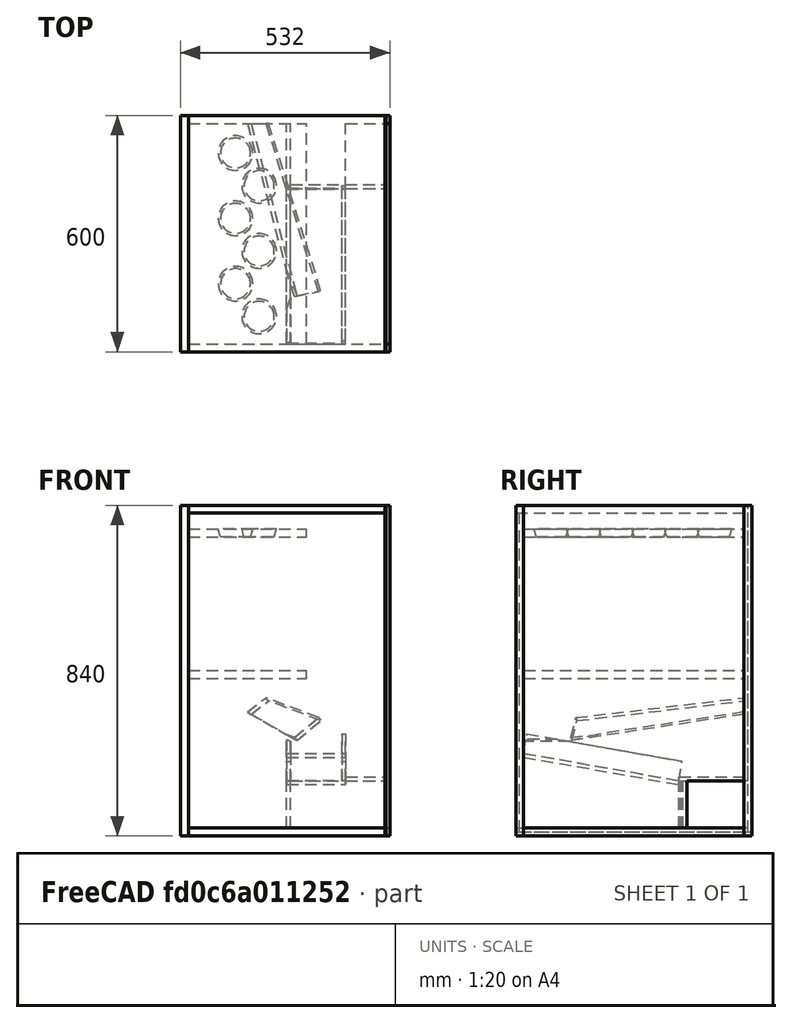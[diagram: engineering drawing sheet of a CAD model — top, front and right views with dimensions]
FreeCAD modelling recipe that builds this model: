
FCSTD DOCUMENT  (FreeCAD 0.16R)
Label: Structure
License: All rights reserved
LicenseURL: http://en.wikipedia.org/wiki/All_rights_reserved
objects: Part::Box×23, Part::FeaturePython×10, Part::Cone×6
note: 39 computed .brp shape members not serialized (recipe doc carries the construction recipe); baked Part::Feature solids carry a one-line shape summary decoded from their .brp

FEATURE [Part::Box] Box  label="bottom"
  Height = 20
  Length = 500
  Width = 600
FEATURE [Part::Box] Box001  label="left"
  Height = 800
  Length = 500
  Placement = pos=(0,0,20) rot=(0,0,1;0rad)
  Width = 20
FEATURE [Part::Box] Box002  label="right"
  Height = 800
  Length = 500
  Placement = pos=(0,580,20) rot=(0,0,1;0rad)
  Width = 20
FEATURE [Part::Box] Box003  label="top"
  Height = 20
  Length = 500
  Placement = pos=(0,0,820) rot=(0,0,1;0rad)
  Width = 600
FEATURE [Part::Box] Box004  label="shelf"
  Height = 20
  Length = 300
  Placement = pos=(0,20,400) rot=(0,0,1;0rad)
  Width = 560
FEATURE [Part::Box] Box006  label="left rail"
  Height = 830
  Length = 2
  Placement = pos=(500,0,10) rot=(0,0,1;0rad)
  Width = 10
FEATURE [Part::Box] Box007  label="right rail"
  Height = 830
  Length = 2
  Placement = pos=(500,590,10) rot=(0,0,1;0rad)
  Width = 10
FEATURE [Part::Box] Box008  label="bottom rail"
  Height = 10
  Length = 2
  Placement = pos=(500,0,0) rot=(0,0,1;0rad)
  Width = 600
FEATURE [Part::Box] Box005  label="pipe"
  Height = 10
  Length = 340
  Placement = pos=(0,20,390) rot=(0,1,0;0.523599rad)
  Width = 560
FEATURE [Part::Box] Box009  label="left rail001"
  Height = 840
  Length = 10
  Placement = pos=(502,0,0) rot=(0,0,1;0rad)
  Width = 20
FEATURE [Part::Box] Box010  label="right rail001"
  Height = 840
  Length = 10
  Placement = pos=(502,580,0) rot=(0,0,1;0rad)
  Width = 20
FEATURE [Part::Box] Box011  label="bottom rail001"
  Height = 20
  Length = 10
  Placement = pos=(502,20,0) rot=(0,0,1;0rad)
  Width = 560
FEATURE [Part::Box] Box012  label="back"
  Height = 840
  Length = 20
  Placement = pos=(-20,0,0) rot=(0,0,1;0rad)
  Width = 600
FEATURE [Part::Box] Box017  label="plexiglass1"
  Height = 830
  Length = 2
  Placement = pos=(500,10,10) rot=(0,0,1;0rad)
  Width = 580
FEATURE [Part::Box] Box018  label="upper_shelf"
  Height = 20
  Length = 300
  Placement = pos=(0,20,760) rot=(0,0,1;0rad)
  Width = 560
FEATURE [Part::Cone] Cone  label="container1"
  Angle = 360
  Height = 100
  Placement = pos=(180,90,700) rot=(0,0,1;0rad)
  Radius1 = 20
  Radius2 = 50
FEATURE [Part::Cone] Cone001  label="container2"
  Angle = 360
  Height = 100
  Placement = pos=(120,173,700) rot=(0,0,1;0rad)
  Radius1 = 20
  Radius2 = 50
FEATURE [Part::Cone] Cone002  label="container3"
  Angle = 360
  Height = 100
  Placement = pos=(180,256,700) rot=(0,0,1;0rad)
  Radius1 = 20
  Radius2 = 50
FEATURE [Part::Cone] Cone003  label="container4"
  Angle = 360
  Height = 100
  Placement = pos=(120,339,700) rot=(0,0,1;0rad)
  Radius1 = 20
  Radius2 = 50
FEATURE [Part::Cone] Cone004  label="container5"
  Angle = 360
  Height = 100
  Placement = pos=(180,422,700) rot=(0,0,1;0rad)
  Radius1 = 20
  Radius2 = 50
FEATURE [Part::Cone] Cone005  label="container6"
  Angle = 360
  Height = 100
  Placement = pos=(120,505,700) rot=(0,0,1;0rad)
  Radius1 = 20
  Radius2 = 50
FEATURE [Part::FeaturePython] Cutout  # WARN: FeaturePython — macro-defined, semantics opaque (R4)
  Base = -> Box018
  Mode = 3
  Tool = -> Cone
FEATURE [Part::FeaturePython] Cutout001  # WARN: FeaturePython — macro-defined, semantics opaque (R4)
  Base = -> Cutout
  Mode = 3
  Tool = -> Cone001
FEATURE [Part::FeaturePython] Cutout002  # WARN: FeaturePython — macro-defined, semantics opaque (R4)
  Base = -> Cutout001
  Mode = 3
  Tool = -> Cone002
FEATURE [Part::FeaturePython] Cutout003  # WARN: FeaturePython — macro-defined, semantics opaque (R4)
  Base = -> Cutout002
  Mode = 3
  Tool = -> Cone003
FEATURE [Part::FeaturePython] Cutout004  # WARN: FeaturePython — macro-defined, semantics opaque (R4)
  Base = -> Cutout003
  Mode = 3
  Tool = -> Cone004
FEATURE [Part::FeaturePython] Cutout005  label="ushelf_containers"  # WARN: FeaturePython — macro-defined, semantics opaque (R4)
  Base = -> Cutout004
  Mode = 3
  Tool = -> Cone005
FEATURE [Part::Box] Box019  label="pipe2"
  Height = 10
  Length = 150
  Placement = pos=(250,20,200) rot=(-1,0,0;0.174533rad)
  Width = 400
FEATURE [Part::Box] Box020  label="pipe3"
  Height = 50
  Length = 10
  Placement = pos=(250,20,210) rot=(-1,0,0;0.174533rad)
  Width = 400
FEATURE [Part::FeaturePython] Cutout006  label="pipe_wall2"  # WARN: FeaturePython — macro-defined, semantics opaque (R4)
  Base = -> Box020
  Mode = 3
  Tool = -> Box005
FEATURE [Part::Box] Box021  label="pipe_wall3"
  Height = 50
  Length = 10
  Placement = pos=(390,20,210) rot=(-1,0,0;0.174533rad)
  Width = 400
FEATURE [Part::Box] Box022  label="pipe_wall"
  Height = 80
  Length = 10
  Placement = pos=(270,140,250) rot=(-0.030642,0.936674,0.34886;0.9494rad)
  Width = 470
FEATURE [Part::Box] Box023  label="handbox_back"
  Height = 120
  Length = 10
  Placement = pos=(250,420,20) rot=(0,0,1;0rad)
  Width = 160
FEATURE [Part::Box] Box024  label="handbox_left"
  Height = 120
  Length = 240
  Placement = pos=(260,415,20) rot=(0,0,1;0rad)
  Width = 10
FEATURE [Part::Box] Box025  label="handbox_top"
  Height = 10
  Length = 100
  Placement = pos=(400,415,140) rot=(0,0,1;0rad)
  Width = 165
FEATURE [Part::Box] Box026  label="Cube"
  Height = 120
  Length = 100
  Placement = pos=(450,435,20) rot=(0,0,1;0rad)
  Width = 155
FEATURE [Part::FeaturePython] Cutout009  label="plexiglass"  # WARN: FeaturePython — macro-defined, semantics opaque (R4)
  Base = -> Box017
  Mode = 3
  Tool = -> Box026
FEATURE [Part::FeaturePython] Cutout010  label="pipewall_right"  # WARN: FeaturePython — macro-defined, semantics opaque (R4)
  Base = -> Box022
  Mode = 3
  Tool = -> Box002
FEATURE [Part::FeaturePython] Cutout011  label="pipe_wall1"  # WARN: FeaturePython — macro-defined, semantics opaque (R4)
  Base = -> Cutout010
  Mode = 3
  Tool = -> Box005
